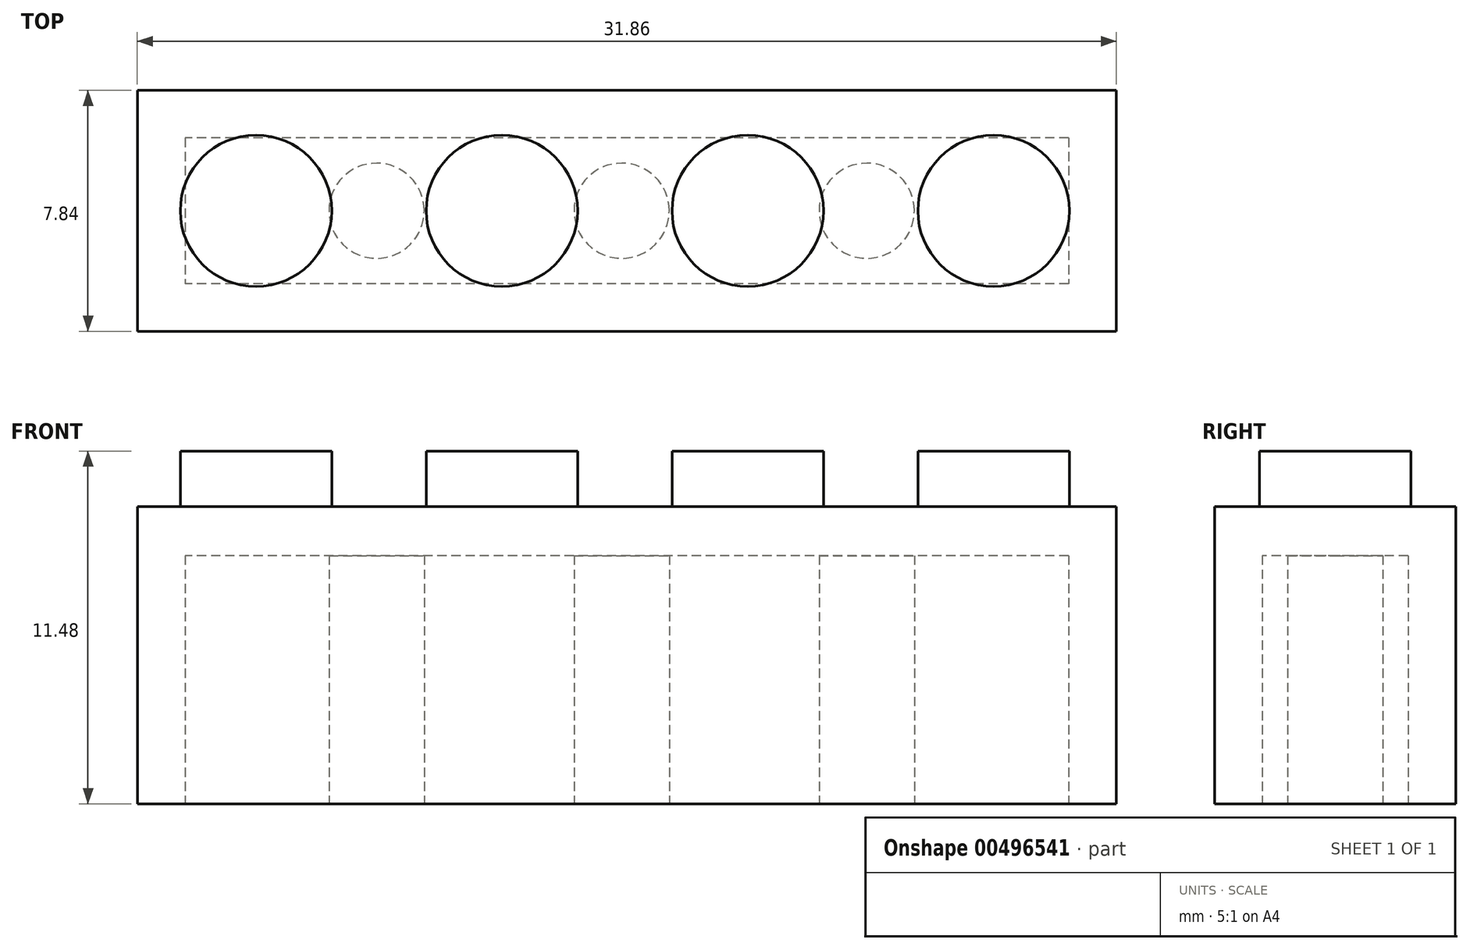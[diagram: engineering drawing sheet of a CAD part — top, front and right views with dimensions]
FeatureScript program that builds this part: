
annotation { "Feature Type Name" : "Feature", "Feature Type Description" : "" }
export const myFeature = defineFeature(function(context is Context, id is Id, definition is map)
    precondition{}
    {
        {
            var Q0;
            Q0=qCreatedBy(makeId("Top.planeOp"),FACE);
            var sketch = newSketch(context, id + "F0", { "sketchPlane" : qUnion([Q0])});
            skLineSegment(sketch, "E0.bottom", {"start": v(15.93, 3.92) * mm, "end": v(-15.93, 3.92) * mm});
            skLineSegment(sketch, "E0.top", {"start": v(15.93, -3.92) * mm, "end": v(-15.93, -3.92) * mm});
            skLineSegment(sketch, "E0.left", {"start": v(15.93, 3.92) * mm, "end": v(15.93, -3.92) * mm});
            skLineSegment(sketch, "E0.right", {"start": v(-15.93, 3.92) * mm, "end": v(-15.93, -3.92) * mm});
            skPoint(sketch, "E0.middle", {"position": v(0, 0) * mm});
            skSolve(sketch);
        }
        {
            var Q0;
            Q0=makeQuery(id+"F0.imprint","IMPRINT",FACE,{"disambiguationData":[TD([[makeQuery(id+"F0.imprint","IMPRINT",EDGE,{"derivedFrom":sQuery(id+"F0.wireOp",EDGE,"E0.bottom")}),1.0]])]});
            extrude(context, id + "F1", {"entities" : qUnion([Q0]), "depth" : 9.68 * mm});
        }
        {
            var Q0;
            Q0=makeQuery(id+"F1.opExtrude","CAP_FACE",FACE,{"disambiguationData":[OSD([sQuery(id+"F0.wireOp",EDGE,"E0.bottom"),sQuery(id+"F0.wireOp",EDGE,"E0.top"),sQuery(id+"F0.wireOp",EDGE,"E0.left"),sQuery(id+"F0.wireOp",EDGE,"E0.right")])],"isStart":false});
            var sketch = newSketch(context, id + "F2", { "sketchPlane" : qUnion([Q0])});
            skCircle(sketch, "E1", {"center": v(-12.07, 0) * mm, "radius": 2.46 * mm});
            skCircle(sketch, "E2.1.0.0", {"center": v(-4.06, 0) * mm, "radius": 2.46 * mm});
            skCircle(sketch, "E2.2.0.0", {"center": v(3.94, 0) * mm, "radius": 2.46 * mm});
            skCircle(sketch, "E2.3.0.0", {"center": v(11.94, 0) * mm, "radius": 2.46 * mm});
            skLineSegment(sketch, "E2.direction1", {"start": v(-12.07, 0) * mm, "end": v(-4.06, 0) * mm, "construction": true});
            skSolve(sketch);
        }
        {
            var Q0;
            Q0=makeQuery(id+"F2.imprint","IMPRINT",FACE,{"disambiguationData":[TD([[makeQuery(id+"F2.imprint","IMPRINT",EDGE,{"derivedFrom":sQuery(id+"F2.wireOp",EDGE,"E2.1.0.0")}),1.0]])]});
            var Q1;
            Q1=makeQuery(id+"F2.imprint","IMPRINT",FACE,{"disambiguationData":[TD([[makeQuery(id+"F2.imprint","IMPRINT",EDGE,{"derivedFrom":sQuery(id+"F2.wireOp",EDGE,"E2.2.0.0")}),1.0]])]});
            var Q2;
            Q2=makeQuery(id+"F2.imprint","IMPRINT",FACE,{"disambiguationData":[TD([[makeQuery(id+"F2.imprint","IMPRINT",EDGE,{"derivedFrom":sQuery(id+"F2.wireOp",EDGE,"E2.3.0.0")}),1.0]])]});
            var Q3;
            Q3=makeQuery(id+"F2.imprint","IMPRINT",FACE,{"disambiguationData":[TD([[makeQuery(id+"F2.imprint","IMPRINT",EDGE,{"derivedFrom":sQuery(id+"F2.wireOp",EDGE,"E1")}),1.0]])]});
            extrude(context, id + "F3", {"entities" : qUnion([Q0, Q1, Q2, Q3]), "operationType" : NewBodyOperationType.ADD, "depth" : 1.8 * mm});
        }
        {
            var Q0;
            Q0=makeQuery(id+"F1.opExtrude","CAP_FACE",FACE,{"disambiguationData":[OSD([sQuery(id+"F0.wireOp",EDGE,"E0.bottom"),sQuery(id+"F0.wireOp",EDGE,"E0.top"),sQuery(id+"F0.wireOp",EDGE,"E0.left"),sQuery(id+"F0.wireOp",EDGE,"E0.right")])],"isStart":true});
            var sketch = newSketch(context, id + "F4", { "sketchPlane" : qUnion([Q0])});
            skCircle(sketch, "E3", {"center": v(-8.14, 0) * mm, "radius": 1.55 * mm});
            skCircle(sketch, "E4.1.0.0", {"center": v(-0.17, 0) * mm, "radius": 1.55 * mm});
            skCircle(sketch, "E4.2.0.0", {"center": v(7.81, 0) * mm, "radius": 1.55 * mm});
            skLineSegment(sketch, "E4.direction1", {"start": v(-8.14, 0) * mm, "end": v(-0.17, 0) * mm, "construction": true});
            skSolve(sketch);
        }
        {
            var Q0;
            Q0=makeQuery(id+"F4.imprint","IMPRINT",FACE,{"disambiguationData":[TD([[makeQuery(id+"F4.imprint","IMPRINT",EDGE,{"derivedFrom":sQuery(id+"F4.wireOp",EDGE,"E3")}),-1.0]])]});
            var sketch = newSketch(context, id + "F5", { "sketchPlane" : qUnion([Q0])});
            skLineSegment(sketch, "E5.bottom", {"start": v(14.38, -2.37) * mm, "end": v(-14.38, -2.37) * mm});
            skLineSegment(sketch, "E5.top", {"start": v(14.38, 2.37) * mm, "end": v(-14.38, 2.37) * mm});
            skLineSegment(sketch, "E5.left", {"start": v(14.38, -2.37) * mm, "end": v(14.38, 2.37) * mm});
            skLineSegment(sketch, "E5.right", {"start": v(-14.38, -2.37) * mm, "end": v(-14.38, 2.37) * mm});
            skPoint(sketch, "E5.middle", {"position": v(0, 0) * mm});
            skSolve(sketch);
        }
        {
            var Q0;
            Q0=makeQuery(id+"F5.imprint","IMPRINT",FACE,{"disambiguationData":[TD([[makeQuery(id+"F5.imprint","IMPRINT",EDGE,{"derivedFrom":sQuery(id+"F5.wireOp",EDGE,"E5.bottom")}),-1.0]])]});
            extrude(context, id + "F6", {"entities" : qUnion([Q0]), "operationType" : NewBodyOperationType.REMOVE, "oppositeDirection" : true, "depth" : 8.08 * mm});
        }
    });
